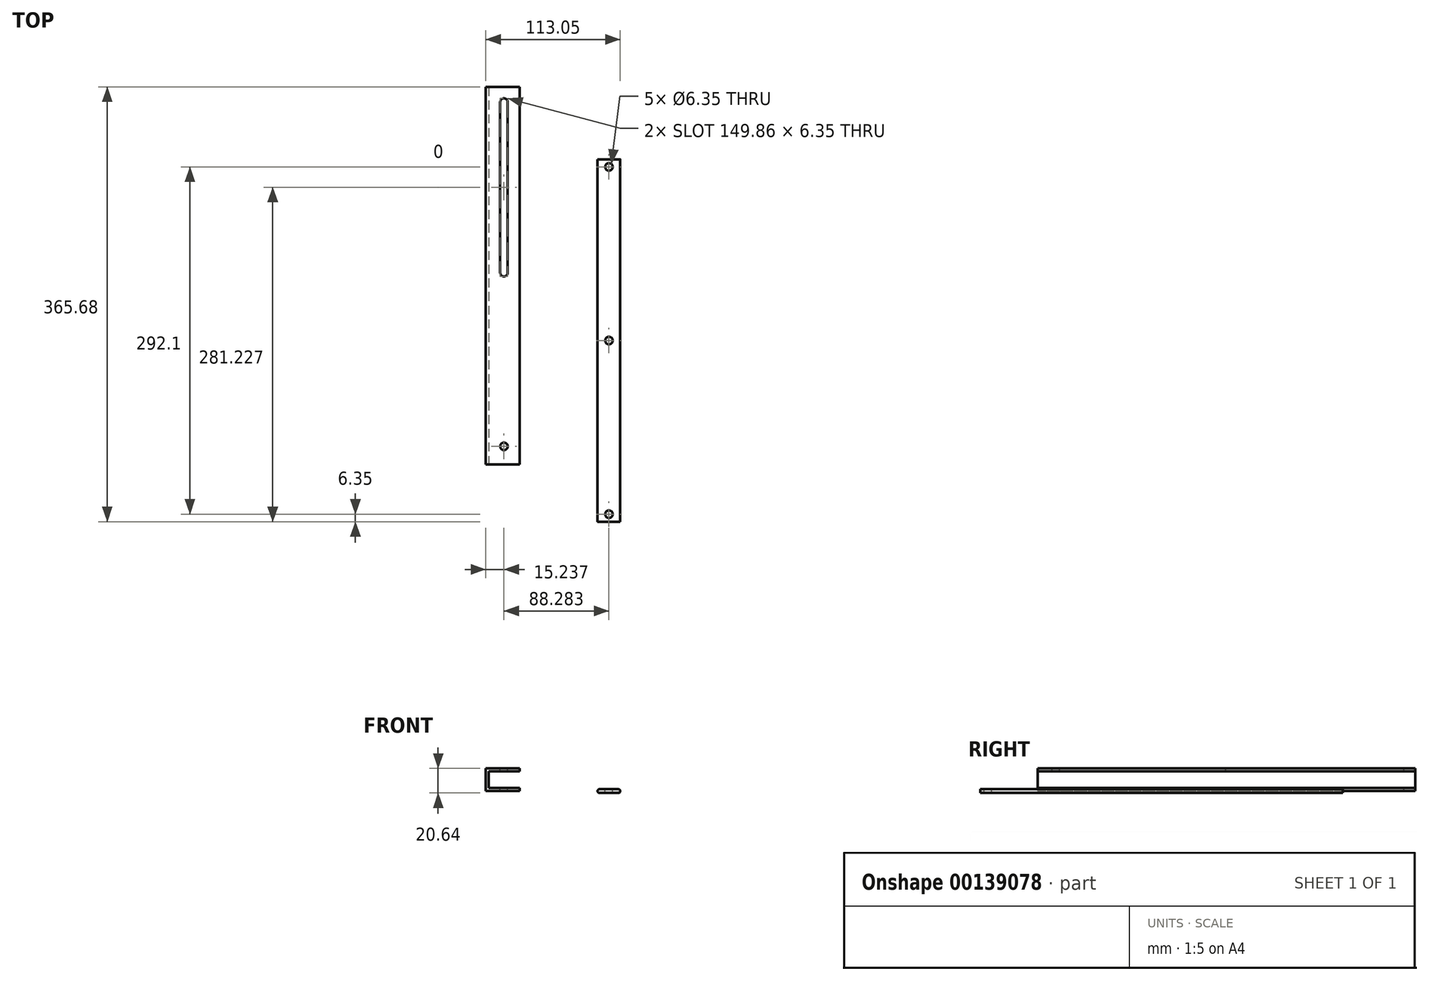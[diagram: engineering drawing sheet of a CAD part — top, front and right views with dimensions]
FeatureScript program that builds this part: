
annotation { "Feature Type Name" : "Feature", "Feature Type Description" : "" }
export const myFeature = defineFeature(function(context is Context, id is Id, definition is map)
    precondition{}
    {
        {
            var Q0;
            Q0=qCreatedBy(makeId("Front.planeOp"),FACE);
            var sketch = newSketch(context, id + "F0", { "sketchPlane" : qUnion([Q0])});
            skLineSegment(sketch, "E0.bottom", {"start": v(-7.94, 1.59) * mm, "end": v(7.94, 1.59) * mm});
            skLineSegment(sketch, "E0.top", {"start": v(-7.94, -1.59) * mm, "end": v(7.94, -1.59) * mm});
            skLineSegment(sketch, "E0.left", {"start": v(-9.53, 0) * mm, "end": v(-9.53, 0) * mm});
            skLineSegment(sketch, "E0.right", {"start": v(9.53, 0) * mm, "end": v(9.53, 0) * mm});
            skPoint(sketch, "E0.middle", {"position": v(0, 0) * mm});
            skPoint(sketch, "E1.visualSharp", {"position": v(-9.53, 1.59) * mm});
            skArc(sketch, "E1.filletArc", {"start": v(-7.94, 1.59) * mm, "mid": v(-9.06, 1.12) * mm, "end": v(-9.53, 0) * mm});
            skPoint(sketch, "E2.visualSharp", {"position": v(-9.53, -1.59) * mm});
            skArc(sketch, "E2.filletArc", {"start": v(-9.53, 0) * mm, "mid": v(-9.06, -1.12) * mm, "end": v(-7.94, -1.59) * mm});
            skPoint(sketch, "E3.visualSharp", {"position": v(9.53, 1.59) * mm});
            skArc(sketch, "E3.filletArc", {"start": v(9.53, 0) * mm, "mid": v(9.06, 1.12) * mm, "end": v(7.94, 1.59) * mm});
            skPoint(sketch, "E4.visualSharp", {"position": v(9.53, -1.59) * mm});
            skArc(sketch, "E4.filletArc", {"start": v(7.94, -1.59) * mm, "mid": v(9.06, -1.12) * mm, "end": v(9.53, 0) * mm});
            skSolve(sketch);
        }
        {
            var Q0;
            Q0=makeQuery(id+"F0.imprint","IMPRINT",FACE,{"disambiguationData":[TD([[makeQuery(id+"F0.imprint","IMPRINT",EDGE,{"derivedFrom":sQuery(id+"F0.wireOp",EDGE,"E0.bottom")}),-1.0]])]});
            extrude(context, id + "F1", {"entities" : qUnion([Q0]), "depth" : 304.8 * mm});
        }
        {
            var Q0;
            Q0=makeQuery(id+"F1.opExtrude","SWEPT_FACE",FACE,{"disambiguationData":[OSD([sQuery(id+"F0.wireOp",EDGE,"E0.bottom")])]});
            var sketch = newSketch(context, id + "F2", { "sketchPlane" : qUnion([Q0])});
            skCircle(sketch, "E5", {"center": v(0, -152.4) * mm, "radius": 3.18 * mm});
            skPoint(sketch, "E5.centerSnap0", {"position": v(-7.94, -152.4) * mm});
            skCircle(sketch, "E6", {"center": v(0, -6.35) * mm, "radius": 3.18 * mm});
            skCircle(sketch, "E7", {"center": v(0, -298.45) * mm, "radius": 3.18 * mm});
            skPoint(sketch, "E7.centerSnap0", {"position": v(0, -304.8) * mm});
            skSolve(sketch);
        }
        {
            var Q0;
            Q0=makeQuery(id+"F2.imprint","IMPRINT",FACE,{"disambiguationData":[TD([[makeQuery(id+"F2.imprint","IMPRINT",EDGE,{"derivedFrom":sQuery(id+"F2.wireOp",EDGE,"E7")}),1.0]])]});
            var Q1;
            Q1=makeQuery(id+"F2.imprint","IMPRINT",FACE,{"disambiguationData":[TD([[makeQuery(id+"F2.imprint","IMPRINT",EDGE,{"derivedFrom":sQuery(id+"F2.wireOp",EDGE,"E5")}),1.0]])]});
            var Q2;
            Q2=makeQuery(id+"F2.imprint","IMPRINT",FACE,{"disambiguationData":[TD([[makeQuery(id+"F2.imprint","IMPRINT",EDGE,{"derivedFrom":sQuery(id+"F2.wireOp",EDGE,"E6")}),1.0]])]});
            extrude(context, id + "F3", {"entities" : qUnion([Q0, Q1, Q2]), "operationType" : NewBodyOperationType.REMOVE, "oppositeDirection" : true, "depth" : 25.4 * mm});
        }
        {
            var Q0;
            Q0=qCreatedBy(makeId("Top.planeOp"),FACE);
            var sketch = newSketch(context, id + "F4", { "sketchPlane" : qUnion([Q0])});
            skLineSegment(sketch, "E8.bottom", {"start": v(-103.52, 60.88) * mm, "end": v(-74.95, 60.88) * mm});
            skLineSegment(sketch, "E8.top", {"start": v(-103.52, -256.62) * mm, "end": v(-74.95, -256.62) * mm});
            skLineSegment(sketch, "E8.left", {"start": v(-103.52, 60.88) * mm, "end": v(-103.52, -256.62) * mm});
            skLineSegment(sketch, "E8.right", {"start": v(-74.95, 60.88) * mm, "end": v(-74.95, -256.62) * mm});
            skSolve(sketch);
        }
        {
            var Q0;
            Q0 = qSketchRegion(id + "F4", true);
            extrude(context, id + "F5", {"entities" : qUnion([Q0]), "depth" : 19.05 * mm});
        }
        {
            var Q0;
            Q0=makeQuery(id+"F5.opExtrude","SWEPT_FACE",FACE,{"disambiguationData":[OSD([sQuery(id+"F4.wireOp",EDGE,"E8.right")])]});
            var Q1;
            Q1=makeQuery(id+"F5.opExtrude","SWEPT_FACE",FACE,{"disambiguationData":[OSD([sQuery(id+"F4.wireOp",EDGE,"E8.top")])]});
            var Q2;
            Q2=makeQuery(id+"F5.opExtrude","SWEPT_FACE",FACE,{"disambiguationData":[OSD([sQuery(id+"F4.wireOp",EDGE,"E8.bottom")])]});
            shell(context, id + "F6", {"entities" : qUnion([Q0, Q1, Q2]), "thickness" : 2.54 * mm});
        }
        {
            var Q0;
            Q0=makeQuery(id+"F5.opExtrude","CAP_FACE",FACE,{"disambiguationData":[OSD([sQuery(id+"F4.wireOp",EDGE,"E8.bottom"),sQuery(id+"F4.wireOp",EDGE,"E8.top"),sQuery(id+"F4.wireOp",EDGE,"E8.left"),sQuery(id+"F4.wireOp",EDGE,"E8.right")])],"isStart":false});
            var sketch = newSketch(context, id + "F7", { "sketchPlane" : qUnion([Q0])});
            skCircle(sketch, "E9", {"center": v(-88.28, -241.38) * mm, "radius": 3.18 * mm});
            skPoint(sketch, "E9.centerSnap0", {"position": v(-88.28, -254.08) * mm});
            skArc(sketch, "E10", {"start": v(-91.46, -95.33) * mm, "mid": v(-88.28, -98.5) * mm, "end": v(-85.1, -95.33) * mm});
            skArc(sketch, "E11", {"start": v(-85.1, 48.18) * mm, "mid": v(-88.28, 51.36) * mm, "end": v(-91.46, 48.18) * mm});
            skLineSegment(sketch, "E12", {"start": v(-103.52, -97.87) * mm, "end": v(-73.04, -92.79) * mm, "construction": true});
            skLineSegment(sketch, "E13", {"start": v(-85.1, -95.33) * mm, "end": v(-85.1, 48.18) * mm});
            skLineSegment(sketch, "E14", {"start": v(-91.46, 48.18) * mm, "end": v(-91.46, -95.33) * mm});
            skSolve(sketch);
        }
        {
            var Q0;
            Q0 = qSketchRegion(id + "F7", true);
            extrude(context, id + "F8", {"entities" : qUnion([Q0]), "operationType" : NewBodyOperationType.REMOVE, "oppositeDirection" : true, "depth" : 25.4 * mm});
        }
    });
